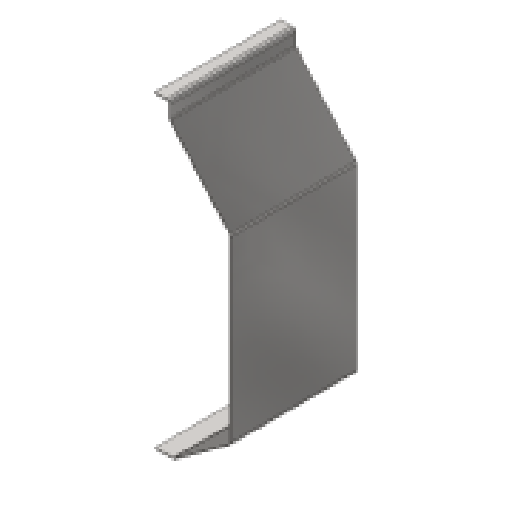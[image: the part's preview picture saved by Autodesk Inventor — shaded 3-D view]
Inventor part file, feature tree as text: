
AUTODESK INVENTOR PART (.ipt)
format: ipt  version: 2025 (Build 290162000, 162)  size: 138,240 bytes
history: native  units: mm
features: reference x13, other x11, fillet x2, extrude x1, sketch x1
ambient origin geometry x8: Origin, YZ Plane, XZ Plane, XY Plane, X Axis, Y Axis, Z Axis, Center Point
bodies: Solid1 (feature_tree)
feature tree (28):
  extrude  "Extrusion1"  Depth=234.0mm TaperAngle=0.0deg
  fillet  "Fillet1"  Radius=5.0mm
  fillet  "Fillet2"  Radius=7.0mm
  sketch  "Sketch1"  dims[d0=1.6256mm d1=234.0mm d2=0.0mm d3=5.0mm d4=7.0mm]
  reference  "Reference1"
  reference  "Reference2"
  reference  "Reference3"
  reference  "Reference4"
  reference  "Reference5"
  reference  "Reference6"
  reference  "Reference7"
  reference  "Reference8"
  reference  "Reference9"
  reference  "Reference10"
  reference  "Reference11"
  reference  "Reference12"
  reference  "Reference13"
  other  "<userpath>\Desktop\puppycat\woodhouseMK1.iam"
  other  "woodhouseMK1.iam"
  other  "10inStrut:2"
  other  "6pt9inStrut:2"
  other  "horizontalStrut:1"
  other  "lowerRearBracketFlipped:1"
  other  "upperRearBracket:1"
  other  "rearStrut:2"
  other  "12inStrut:1"
  other  "idlerBaseV1:4"
  other  "trackBase:2"
